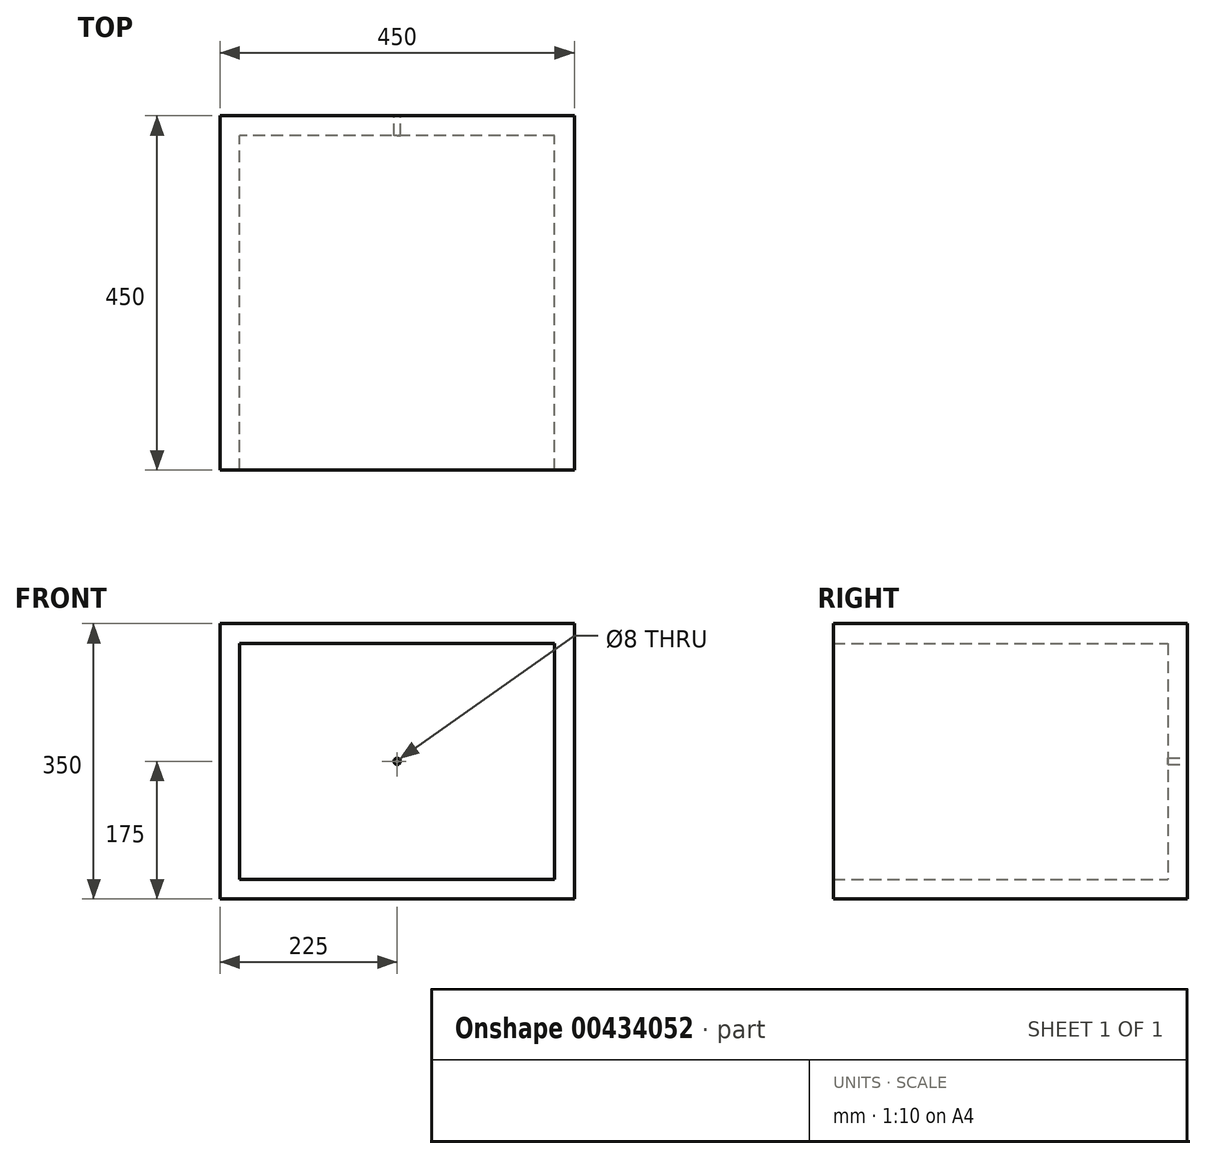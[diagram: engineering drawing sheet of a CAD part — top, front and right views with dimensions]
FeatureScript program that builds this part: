
annotation { "Feature Type Name" : "Feature", "Feature Type Description" : "" }
export const myFeature = defineFeature(function(context is Context, id is Id, definition is map)
    precondition{}
    {
        {
            var Q0;
            Q0=qCreatedBy(makeId("Front.planeOp"),FACE);
            var sketch = newSketch(context, id + "F0", { "sketchPlane" : qUnion([Q0])});
            skLineSegment(sketch, "E0.bottom", {"start": v(225, 175) * mm, "end": v(-225, 175) * mm});
            skLineSegment(sketch, "E0.top", {"start": v(225, -175) * mm, "end": v(-225, -175) * mm});
            skLineSegment(sketch, "E0.left", {"start": v(225, 175) * mm, "end": v(225, -175) * mm});
            skLineSegment(sketch, "E0.right", {"start": v(-225, 175) * mm, "end": v(-225, -175) * mm});
            skPoint(sketch, "E0.middle", {"position": v(0, 0) * mm});
            skSolve(sketch);
        }
        {
            var Q0;
            Q0 = qSketchRegion(id + "F0", true);
            extrude(context, id + "F1", {"entities" : qUnion([Q0]), "depth" : 450 * mm});
        }
        {
            var Q0;
            Q0=makeQuery(id+"F1.opExtrude","CAP_FACE",FACE,{"disambiguationData":[OSD([sQuery(id+"F0.wireOp",EDGE,"E0.bottom"),sQuery(id+"F0.wireOp",EDGE,"E0.top"),sQuery(id+"F0.wireOp",EDGE,"E0.left"),sQuery(id+"F0.wireOp",EDGE,"E0.right")])],"isStart":false});
            shell(context, id + "F2", {"entities" : qUnion([Q0]), "thickness" : 25 * mm});
        }
        {
            var Q0;
            Q0=makeQuery(id+"F1.opExtrude","CAP_FACE",FACE,{"disambiguationData":[OSD([sQuery(id+"F0.wireOp",EDGE,"E0.bottom"),sQuery(id+"F0.wireOp",EDGE,"E0.top"),sQuery(id+"F0.wireOp",EDGE,"E0.left"),sQuery(id+"F0.wireOp",EDGE,"E0.right")])],"isStart":true});
            var sketch = newSketch(context, id + "F3", { "sketchPlane" : qUnion([Q0])});
            skCircle(sketch, "E1", {"center": v(0, 0) * mm, "radius": 4 * mm});
            skSolve(sketch);
        }
        {
            var Q0;
            Q0 = qSketchRegion(id + "F3", true);
            extrude(context, id + "F4", {"entities" : qUnion([Q0]), "operationType" : NewBodyOperationType.REMOVE, "endBound" : BoundingType.THROUGH_ALL, "oppositeDirection" : true, "depth" : 25 * mm});
        }
    });
